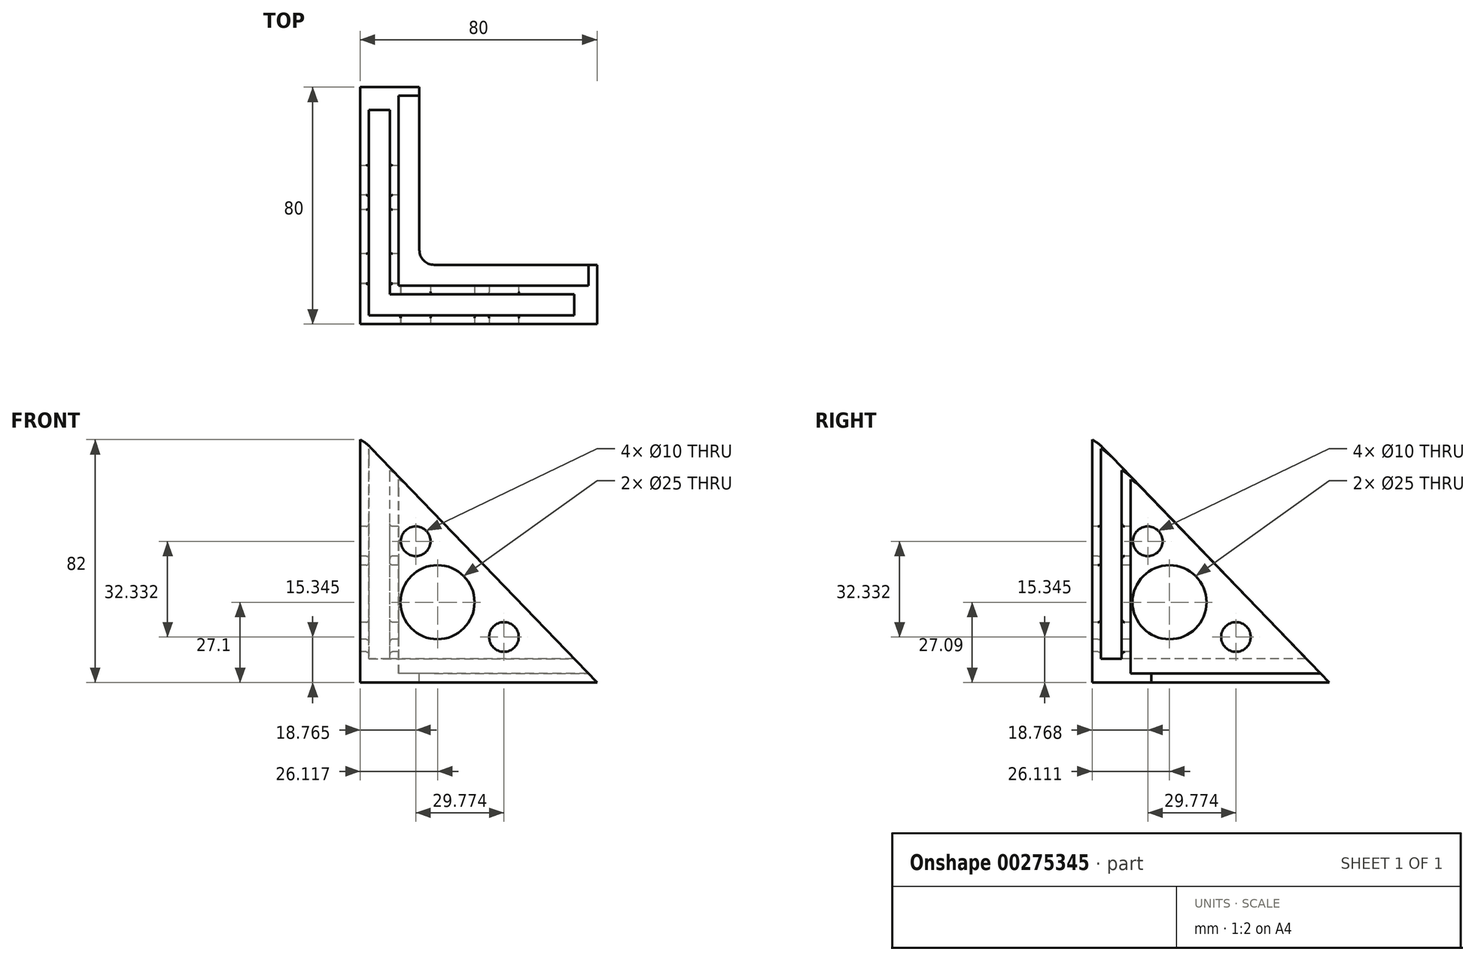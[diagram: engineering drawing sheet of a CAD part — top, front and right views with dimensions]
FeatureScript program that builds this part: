
annotation { "Feature Type Name" : "Feature", "Feature Type Description" : "" }
export const myFeature = defineFeature(function(context is Context, id is Id, definition is map)
    precondition{}
    {
        {
            var Q0;
            Q0=qCreatedBy(makeId("Top.planeOp"),FACE);
            var sketch = newSketch(context, id + "F0", { "sketchPlane" : qUnion([Q0])});
            skLineSegment(sketch, "E0", {"start": v(-54.23, 39.63) * mm, "end": v(-54.23, -40.37) * mm});
            skLineSegment(sketch, "E1", {"start": v(-54.23, -40.37) * mm, "end": v(25.77, -40.37) * mm});
            skLineSegment(sketch, "E2", {"start": v(-54.23, 39.63) * mm, "end": v(-41.23, 39.63) * mm});
            skLineSegment(sketch, "E3", {"start": v(25.77, -40.37) * mm, "end": v(25.77, -27.37) * mm});
            skLineSegment(sketch, "E4", {"start": v(25.77, -27.37) * mm, "end": v(-41.23, -27.37) * mm});
            skLineSegment(sketch, "E5", {"start": v(-41.23, -27.37) * mm, "end": v(-41.23, 39.63) * mm});
            skSolve(sketch);
        }
        {
            var Q0;
            Q0=qSketchRegion(id+"F0",true);
            extrude(context, id + "F1", {"entities" : qUnion([Q0]), "oppositeDirection" : true, "depth" : 80 * mm});
        }
        {
            var Q0;
            Q0=makeQuery(id+"F1.opExtrude","CAP_FACE",FACE,{"disambiguationData":[OSD([sQuery(id+"F0.wireOp",EDGE,"E0"),sQuery(id+"F0.wireOp",EDGE,"E1"),sQuery(id+"F0.wireOp",EDGE,"E2"),sQuery(id+"F0.wireOp",EDGE,"E3"),sQuery(id+"F0.wireOp",EDGE,"E4"),sQuery(id+"F0.wireOp",EDGE,"E5")])],"isStart":true});
            var sketch = newSketch(context, id + "F2", { "sketchPlane" : qUnion([Q0])});
            skLineSegment(sketch, "E6", {"start": v(-51.23, 39.63) * mm, "end": v(-51.23, -37.37) * mm});
            skLineSegment(sketch, "E7", {"start": v(-51.23, -37.37) * mm, "end": v(25.77, -37.37) * mm});
            skLineSegment(sketch, "E8", {"start": v(25.77, -37.37) * mm, "end": v(25.77, -30.37) * mm});
            skLineSegment(sketch, "E9", {"start": v(25.77, -30.37) * mm, "end": v(-44.23, -30.37) * mm});
            skLineSegment(sketch, "E10", {"start": v(-44.23, -30.37) * mm, "end": v(-44.23, 39.63) * mm});
            skLineSegment(sketch, "E11", {"start": v(-44.23, 39.63) * mm, "end": v(-51.23, 39.63) * mm});
            skSolve(sketch);
        }
        {
            var Q0;
            Q0=qSketchRegion(id+"F2",true);
            extrude(context, id + "F3", {"entities" : qUnion([Q0]), "operationType" : NewBodyOperationType.REMOVE, "oppositeDirection" : true, "depth" : 75 * mm});
        }
        {
            var Q0;
            Q0=makeQuery(id+"F1.opExtrude","SWEPT_FACE",FACE,{"disambiguationData":[OSD([sQuery(id+"F0.wireOp",EDGE,"E3")])]});
            var sketch = newSketch(context, id + "F4", { "sketchPlane" : qUnion([Q0])});
            skLineSegment(sketch, "E12.bottom", {"start": v(-40.37, -80) * mm, "end": v(-27.37, -80) * mm});
            skLineSegment(sketch, "E12.top", {"start": v(-40.37, -80) * mm, "end": v(-27.37, -80) * mm});
            skLineSegment(sketch, "E12.left", {"start": v(-40.37, -80) * mm, "end": v(-40.37, -80) * mm});
            skLineSegment(sketch, "E12.right", {"start": v(-27.37, -80) * mm, "end": v(-27.37, -80) * mm});
            skLineSegment(sketch, "E13.bottom", {"start": v(-20.37, -80) * mm, "end": v(-40.37, -80) * mm});
            skLineSegment(sketch, "E13.top", {"start": v(9.63, -93) * mm, "end": v(-40.37, -93) * mm});
            skLineSegment(sketch, "E13.right", {"start": v(-40.37, -80) * mm, "end": v(-40.37, -93) * mm});
            skLineSegment(sketch, "E14", {"start": v(-35.37, -83) * mm, "end": v(-35.37, -90) * mm});
            skLineSegment(sketch, "E15", {"start": v(-35.37, -90) * mm, "end": v(9.63, -90) * mm});
            skLineSegment(sketch, "E16", {"start": v(9.63, -90) * mm, "end": v(9.63, -93) * mm});
            skLineSegment(sketch, "E17", {"start": v(-20.37, -80) * mm, "end": v(-20.37, -83) * mm});
            skLineSegment(sketch, "E18", {"start": v(-20.37, -83) * mm, "end": v(-35.37, -83) * mm});
            skSolve(sketch);
        }
        {
            var Q0;
            Q0=qSketchRegion(id+"F4",true);
            extrude(context, id + "F5", {"entities" : qUnion([Q0]), "operationType" : NewBodyOperationType.ADD, "oppositeDirection" : true, "depth" : 80 * mm});
        }
        {
            var Q0;
            Q0=makeQuery(id+"F1.opExtrude","SWEPT_FACE",FACE,{"disambiguationData":[OSD([sQuery(id+"F0.wireOp",EDGE,"E2")])]});
            var sketch = newSketch(context, id + "F6", { "sketchPlane" : qUnion([Q0])});
            skLineSegment(sketch, "E19.bottom", {"start": v(34.23, -80) * mm, "end": v(54.23, -80) * mm});
            skLineSegment(sketch, "E19.top", {"start": v(41.23, -93) * mm, "end": v(54.23, -93) * mm});
            skLineSegment(sketch, "E19.right", {"start": v(54.23, -80) * mm, "end": v(54.23, -93) * mm});
            skLineSegment(sketch, "E20", {"start": v(34.23, -80) * mm, "end": v(34.23, -83) * mm});
            skLineSegment(sketch, "E21", {"start": v(34.23, -83) * mm, "end": v(49.23, -83) * mm});
            skLineSegment(sketch, "E22", {"start": v(49.23, -83) * mm, "end": v(49.23, -90) * mm});
            skLineSegment(sketch, "E23", {"start": v(49.23, -90) * mm, "end": v(5.33, -90) * mm});
            skLineSegment(sketch, "E24", {"start": v(5.33, -90) * mm, "end": v(5.33, -93) * mm});
            skLineSegment(sketch, "E25", {"start": v(5.33, -93) * mm, "end": v(41.23, -93) * mm});
            skSolve(sketch);
        }
        {
            var Q0;
            Q0=qSketchRegion(id+"F6",true);
            extrude(context, id + "F7", {"entities" : qUnion([Q0]), "operationType" : NewBodyOperationType.ADD, "oppositeDirection" : true, "depth" : 80 * mm});
        }
        {
            var Q0;
            Q0=makeQuery(id+"F7.boolean.opBoolean","MERGE",FACE,{"derivedFrom":[makeQuery(id+"F5.opExtrude","SWEPT_FACE",FACE,{"disambiguationData":[OSD([sQuery(id+"F4.wireOp",EDGE,"E18")])]}),makeQuery(id+"F7.opExtrude","SWEPT_FACE",FACE,{"disambiguationData":[OSD([sQuery(id+"F6.wireOp",EDGE,"E21")])]})]});
            cPlane(context, id + "F8", {"entities" : qUnion([Q0]), "cplaneType" : CPlaneType.OFFSET, "offset" : 0 * mm, "width" : 150 * mm, "height" : 150 * mm});
        }
        {
            var Q0;
            Q0=qCreatedBy(id+"F8.planeOp",FACE);
            var sketch = newSketch(context, id + "F9", { "sketchPlane" : qUnion([Q0])});
            skLineSegment(sketch, "E26.bottom", {"start": v(29.9, 62.36) * mm, "end": v(-66.47, 62.36) * mm});
            skLineSegment(sketch, "E26.top", {"start": v(29.9, -86.56) * mm, "end": v(-66.47, -86.56) * mm});
            skLineSegment(sketch, "E26.left", {"start": v(29.9, 62.36) * mm, "end": v(29.9, -86.56) * mm});
            skLineSegment(sketch, "E26.right", {"start": v(-66.47, 62.36) * mm, "end": v(-66.47, -86.56) * mm});
            skSolve(sketch);
        }
        {
            var Q0;
            Q0=makeQuery(id+"F9.imprint","IMPRINT",FACE,{"disambiguationData":[TD([[makeQuery(id+"F9.imprint","IMPRINT",EDGE,{"derivedFrom":sQuery(id+"F9.wireOp",EDGE,"E26.bottom")}),1.0]])]});
            extrude(context, id + "F10", {"entities" : qUnion([Q0]), "operationType" : NewBodyOperationType.REMOVE, "depth" : 25 * mm});
        }
        {
            var Q0;
            Q0=makeQuery(id+"F5.boolean.opBoolean","MERGE",FACE,{"derivedFrom":[makeQuery(id+"F1.opExtrude","SWEPT_FACE",FACE,{"disambiguationData":[OSD([sQuery(id+"F0.wireOp",EDGE,"E1")])]}),makeQuery(id+"F5.opExtrude","SWEPT_FACE",FACE,{"disambiguationData":[OSD([sQuery(id+"F4.wireOp",EDGE,"E13.right")])]})]});
            var sketch = newSketch(context, id + "F11", { "sketchPlane" : qUnion([Q0])});
            skLineSegment(sketch, "E27", {"start": v(-54.23, 0) * mm, "end": v(25.77, -83) * mm});
            skLineSegment(sketch, "E28", {"start": v(25.77, -83) * mm, "end": v(25.77, 0) * mm});
            skLineSegment(sketch, "E29", {"start": v(25.77, 0) * mm, "end": v(-54.23, 0) * mm});
            skLineSegment(sketch, "E30", {"start": v(-54.23, -83) * mm, "end": v(-14.23, -41.5) * mm});
            skCircle(sketch, "E31", {"center": v(-28.11, -55.9) * mm, "radius": 12.5 * mm});
            skCircle(sketch, "E32", {"center": v(-35.46, -35.32) * mm, "radius": 5 * mm});
            skCircle(sketch, "E33", {"center": v(-5.7, -67.66) * mm, "radius": 5 * mm});
            skSolve(sketch);
        }
        {
            var Q0;
            Q0 = qSketchRegion(id + "F11", true);
            extrude(context, id + "F12", {"entities" : qUnion([Q0]), "operationType" : NewBodyOperationType.REMOVE, "oppositeDirection" : true, "depth" : 13 * mm});
        }
        {
            var Q0;
            {var subQ2=sQuery(id+"F11.wireOp",EDGE,"E27");Q0=makeQuery(id+"F12.boolean.opBoolean","COPY",FACE,{"disambiguationData":[TD([makeQuery(id+"F1.opExtrude","SWEPT_FACE",FACE,{"disambiguationData":[OSD([sQuery(id+"F0.wireOp",EDGE,"E3")])]})])],"derivedFrom":makeQuery(id+"F12.opExtrude","CAP_FACE",FACE,{"disambiguationData":[OSD([subQ2,sQuery(id+"F11.wireOp",EDGE,"E28"),sQuery(id+"F11.wireOp",EDGE,"E29")])],"isStart":false})});}
            var sketch = newSketch(context, id + "F13", { "sketchPlane" : qUnion([Q0])});
            skLineSegment(sketch, "E34", {"start": v(22.88, -80) * mm, "end": v(25.77, -80) * mm});
            skLineSegment(sketch, "E35", {"start": v(25.77, -80) * mm, "end": v(25.77, -83) * mm});
            skLineSegment(sketch, "E36", {"start": v(25.77, -83) * mm, "end": v(22.88, -80) * mm});
            skSolve(sketch);
        }
        {
            var Q0;
            Q0 = qSketchRegion(id + "F13", true);
            extrude(context, id + "F14", {"entities" : qUnion([Q0]), "operationType" : NewBodyOperationType.REMOVE, "oppositeDirection" : true, "depth" : 25 * mm});
        }
        {
            var Q0;
            Q0=makeQuery(id+"F7.boolean.opBoolean","MERGE",FACE,{"derivedFrom":[makeQuery(id+"F5.boolean.opBoolean","MERGE",FACE,{"derivedFrom":[makeQuery(id+"F1.opExtrude","SWEPT_FACE",FACE,{"disambiguationData":[OSD([sQuery(id+"F0.wireOp",EDGE,"E0")])]}),makeQuery(id+"F5.opExtrude","CAP_FACE",FACE,{"disambiguationData":[OSD([sQuery(id+"F4.wireOp",EDGE,"E13.bottom"),sQuery(id+"F4.wireOp",EDGE,"E13.top"),sQuery(id+"F4.wireOp",EDGE,"E13.right"),sQuery(id+"F4.wireOp",EDGE,"E14"),sQuery(id+"F4.wireOp",EDGE,"E15"),sQuery(id+"F4.wireOp",EDGE,"E16"),sQuery(id+"F4.wireOp",EDGE,"E17"),sQuery(id+"F4.wireOp",EDGE,"E18")])],"isStart":false})]}),makeQuery(id+"F7.opExtrude","SWEPT_FACE",FACE,{"disambiguationData":[OSD([sQuery(id+"F6.wireOp",EDGE,"E19.right")])]})]});
            var sketch = newSketch(context, id + "F15", { "sketchPlane" : qUnion([Q0])});
            skLineSegment(sketch, "E37", {"start": v(40.37, 0) * mm, "end": v(-39.63, -83) * mm});
            skLineSegment(sketch, "E38", {"start": v(-39.63, -83) * mm, "end": v(-39.63, 0) * mm});
            skLineSegment(sketch, "E39", {"start": v(-39.63, 0) * mm, "end": v(40.37, 0) * mm});
            skLineSegment(sketch, "E40", {"start": v(40.37, -83) * mm, "end": v(-39.63, 0) * mm});
            skCircle(sketch, "E41", {"center": v(14.26, -55.9) * mm, "radius": 12.5 * mm});
            skCircle(sketch, "E42", {"center": v(-8.17, -67.66) * mm, "radius": 5 * mm});
            skCircle(sketch, "E43", {"center": v(21.6, -35.32) * mm, "radius": 5 * mm});
            skSolve(sketch);
        }
        {
            var Q0;
            Q0 = qSketchRegion(id + "F15", true);
            extrude(context, id + "F16", {"entities" : qUnion([Q0]), "operationType" : NewBodyOperationType.REMOVE, "oppositeDirection" : true, "depth" : 13 * mm});
        }
        {
            var Q0;
            Q0=makeQuery(id+"F16.boolean.opBoolean","COPY",FACE,{"derivedFrom":makeQuery(id+"F16.opExtrude","CAP_FACE",FACE,{"disambiguationData":[OSD([sQuery(id+"F15.wireOp",EDGE,"E37"),sQuery(id+"F15.wireOp",EDGE,"E38"),sQuery(id+"F15.wireOp",EDGE,"E39")])],"isStart":false})});
            var sketch = newSketch(context, id + "F17", { "sketchPlane" : qUnion([Q0])});
            skLineSegment(sketch, "E44", {"start": v(-39.63, -83) * mm, "end": v(-39.63, -80) * mm});
            skLineSegment(sketch, "E45", {"start": v(-39.63, -80) * mm, "end": v(-36.74, -80) * mm});
            skLineSegment(sketch, "E46", {"start": v(-36.74, -80) * mm, "end": v(-39.63, -83) * mm});
            skSolve(sketch);
        }
        {
            var Q0;
            Q0 = qSketchRegion(id + "F17", true);
            extrude(context, id + "F18", {"entities" : qUnion([Q0]), "operationType" : NewBodyOperationType.REMOVE, "oppositeDirection" : true, "depth" : 25 * mm});
        }
        {
            var Q0;
            Q0=makeQuery(id+"F16.boolean.opBoolean","INTERSECT",EDGE,{"disambiguationData":[OD(1.0)],"derivedFrom":[makeQuery(id+"F14.boolean.opBoolean","MERGE",FACE,{"derivedFrom":[makeQuery(id+"F12.boolean.opBoolean","COPY",FACE,{"derivedFrom":makeQuery(id+"F12.opExtrude","SWEPT_FACE",FACE,{"disambiguationData":[OSD([sQuery(id+"F11.wireOp",EDGE,"E27")])]})}),makeQuery(id+"F14.opExtrude","SWEPT_FACE",FACE,{"disambiguationData":[OSD([sQuery(id+"F13.wireOp",EDGE,"E36")])]})]}),makeQuery(id+"F16.opExtrude","SWEPT_FACE",FACE,{"disambiguationData":[OSD([sQuery(id+"F15.wireOp",EDGE,"E37")])]})]});
            var Q1;
            Q1=makeQuery(id+"F16.boolean.opBoolean","INTERSECT",EDGE,{"disambiguationData":[OD(0.0)],"derivedFrom":[makeQuery(id+"F14.boolean.opBoolean","MERGE",FACE,{"derivedFrom":[makeQuery(id+"F12.boolean.opBoolean","COPY",FACE,{"derivedFrom":makeQuery(id+"F12.opExtrude","SWEPT_FACE",FACE,{"disambiguationData":[OSD([sQuery(id+"F11.wireOp",EDGE,"E27")])]})}),makeQuery(id+"F14.opExtrude","SWEPT_FACE",FACE,{"disambiguationData":[OSD([sQuery(id+"F13.wireOp",EDGE,"E36")])]})]}),makeQuery(id+"F16.opExtrude","SWEPT_FACE",FACE,{"disambiguationData":[OSD([sQuery(id+"F15.wireOp",EDGE,"E37")])]})]});
            var Q2;
            Q2=makeQuery(id+"F7.boolean.opBoolean","INTERSECT",EDGE,{"derivedFrom":[makeQuery(id+"F5.opExtrude","SWEPT_FACE",FACE,{"disambiguationData":[OSD([sQuery(id+"F4.wireOp",EDGE,"E17")])]}),makeQuery(id+"F7.opExtrude","SWEPT_FACE",FACE,{"disambiguationData":[OSD([sQuery(id+"F6.wireOp",EDGE,"E20")])]})]});
            fillet(context, id + "F19", {"entities" : qUnion([Q0, Q1, Q2]), "radius" : 5 * mm, "tangentPropagation" : true, "allowEdgeOverflow" : false});
        }
        {
            var Q0;
            Q0=makeQuery(id+"F12.boolean.opBoolean","COPY",EDGE,{"derivedFrom":makeQuery(id+"F12.opExtrude","CAP_EDGE",EDGE,{"disambiguationData":[OSD([sQuery(id+"F11.wireOp",EDGE,"E32")])],"isStart":false})});
            var Q1;
            Q1=makeQuery(id+"F16.boolean.opBoolean","COPY",EDGE,{"derivedFrom":makeQuery(id+"F16.opExtrude","CAP_EDGE",EDGE,{"disambiguationData":[OSD([sQuery(id+"F15.wireOp",EDGE,"E43")])],"isStart":false})});
            var Q2;
            Q2=makeQuery(id+"F12.boolean.opBoolean","INTERSECT",EDGE,{"derivedFrom":[makeQuery(id+"F3.boolean.opBoolean","COPY",FACE,{"derivedFrom":makeQuery(id+"F3.opExtrude","SWEPT_FACE",FACE,{"disambiguationData":[OSD([sQuery(id+"F2.wireOp",EDGE,"E9")])]})}),makeQuery(id+"F12.opExtrude","SWEPT_FACE",FACE,{"disambiguationData":[OSD([sQuery(id+"F11.wireOp",EDGE,"E32")])]})]});
            var Q3;
            Q3=makeQuery(id+"F16.boolean.opBoolean","INTERSECT",EDGE,{"derivedFrom":[makeQuery(id+"F3.boolean.opBoolean","COPY",FACE,{"derivedFrom":makeQuery(id+"F3.opExtrude","SWEPT_FACE",FACE,{"disambiguationData":[OSD([sQuery(id+"F2.wireOp",EDGE,"E10")])]})}),makeQuery(id+"F16.opExtrude","SWEPT_FACE",FACE,{"disambiguationData":[OSD([sQuery(id+"F15.wireOp",EDGE,"E43")])]})]});
            var Q4;
            Q4=makeQuery(id+"F12.boolean.opBoolean","INTERSECT",EDGE,{"derivedFrom":[makeQuery(id+"F3.boolean.opBoolean","COPY",FACE,{"derivedFrom":makeQuery(id+"F3.opExtrude","SWEPT_FACE",FACE,{"disambiguationData":[OSD([sQuery(id+"F2.wireOp",EDGE,"E7")])]})}),makeQuery(id+"F12.opExtrude","SWEPT_FACE",FACE,{"disambiguationData":[OSD([sQuery(id+"F11.wireOp",EDGE,"E31")])]})]});
            var Q5;
            Q5=makeQuery(id+"F12.boolean.opBoolean","COPY",EDGE,{"derivedFrom":makeQuery(id+"F12.opExtrude","CAP_EDGE",EDGE,{"disambiguationData":[OSD([sQuery(id+"F11.wireOp",EDGE,"E31")])],"isStart":false})});
            var Q6;
            Q6=makeQuery(id+"F16.boolean.opBoolean","COPY",EDGE,{"derivedFrom":makeQuery(id+"F16.opExtrude","CAP_EDGE",EDGE,{"disambiguationData":[OSD([sQuery(id+"F15.wireOp",EDGE,"E41")])],"isStart":false})});
            var Q7;
            Q7=makeQuery(id+"F16.boolean.opBoolean","INTERSECT",EDGE,{"derivedFrom":[makeQuery(id+"F3.boolean.opBoolean","COPY",FACE,{"derivedFrom":makeQuery(id+"F3.opExtrude","SWEPT_FACE",FACE,{"disambiguationData":[OSD([sQuery(id+"F2.wireOp",EDGE,"E10")])]})}),makeQuery(id+"F16.opExtrude","SWEPT_FACE",FACE,{"disambiguationData":[OSD([sQuery(id+"F15.wireOp",EDGE,"E41")])]})]});
            var Q8;
            Q8=makeQuery(id+"F16.boolean.opBoolean","INTERSECT",EDGE,{"derivedFrom":[makeQuery(id+"F3.boolean.opBoolean","COPY",FACE,{"derivedFrom":makeQuery(id+"F3.opExtrude","SWEPT_FACE",FACE,{"disambiguationData":[OSD([sQuery(id+"F2.wireOp",EDGE,"E6")])]})}),makeQuery(id+"F16.opExtrude","SWEPT_FACE",FACE,{"disambiguationData":[OSD([sQuery(id+"F15.wireOp",EDGE,"E41")])]})]});
            var Q9;
            Q9=makeQuery(id+"F16.boolean.opBoolean","COPY",EDGE,{"derivedFrom":makeQuery(id+"F16.opExtrude","CAP_EDGE",EDGE,{"disambiguationData":[OSD([sQuery(id+"F15.wireOp",EDGE,"E41")])],"isStart":true})});
            var Q10;
            Q10=makeQuery(id+"F12.boolean.opBoolean","COPY",EDGE,{"derivedFrom":makeQuery(id+"F12.opExtrude","CAP_EDGE",EDGE,{"disambiguationData":[OSD([sQuery(id+"F11.wireOp",EDGE,"E31")])],"isStart":true})});
            var Q11;
            Q11=makeQuery(id+"F16.boolean.opBoolean","COPY",EDGE,{"derivedFrom":makeQuery(id+"F16.opExtrude","CAP_EDGE",EDGE,{"disambiguationData":[OSD([sQuery(id+"F15.wireOp",EDGE,"E42")])],"isStart":true})});
            var Q12;
            Q12=makeQuery(id+"F16.boolean.opBoolean","INTERSECT",EDGE,{"derivedFrom":[makeQuery(id+"F3.boolean.opBoolean","COPY",FACE,{"derivedFrom":makeQuery(id+"F3.opExtrude","SWEPT_FACE",FACE,{"disambiguationData":[OSD([sQuery(id+"F2.wireOp",EDGE,"E6")])]})}),makeQuery(id+"F16.opExtrude","SWEPT_FACE",FACE,{"disambiguationData":[OSD([sQuery(id+"F15.wireOp",EDGE,"E42")])]})]});
            var Q13;
            Q13=makeQuery(id+"F16.boolean.opBoolean","INTERSECT",EDGE,{"derivedFrom":[makeQuery(id+"F3.boolean.opBoolean","COPY",FACE,{"derivedFrom":makeQuery(id+"F3.opExtrude","SWEPT_FACE",FACE,{"disambiguationData":[OSD([sQuery(id+"F2.wireOp",EDGE,"E10")])]})}),makeQuery(id+"F16.opExtrude","SWEPT_FACE",FACE,{"disambiguationData":[OSD([sQuery(id+"F15.wireOp",EDGE,"E42")])]})]});
            var Q14;
            Q14=makeQuery(id+"F16.boolean.opBoolean","COPY",EDGE,{"derivedFrom":makeQuery(id+"F16.opExtrude","CAP_EDGE",EDGE,{"disambiguationData":[OSD([sQuery(id+"F15.wireOp",EDGE,"E42")])],"isStart":false})});
            var Q15;
            Q15=makeQuery(id+"F12.boolean.opBoolean","INTERSECT",EDGE,{"derivedFrom":[makeQuery(id+"F3.boolean.opBoolean","COPY",FACE,{"derivedFrom":makeQuery(id+"F3.opExtrude","SWEPT_FACE",FACE,{"disambiguationData":[OSD([sQuery(id+"F2.wireOp",EDGE,"E7")])]})}),makeQuery(id+"F12.opExtrude","SWEPT_FACE",FACE,{"disambiguationData":[OSD([sQuery(id+"F11.wireOp",EDGE,"E33")])]})]});
            var Q16;
            Q16=makeQuery(id+"F12.boolean.opBoolean","COPY",EDGE,{"derivedFrom":makeQuery(id+"F12.opExtrude","CAP_EDGE",EDGE,{"disambiguationData":[OSD([sQuery(id+"F11.wireOp",EDGE,"E33")])],"isStart":true})});
            var Q17;
            Q17=makeQuery(id+"F12.boolean.opBoolean","INTERSECT",EDGE,{"derivedFrom":[makeQuery(id+"F3.boolean.opBoolean","COPY",FACE,{"derivedFrom":makeQuery(id+"F3.opExtrude","SWEPT_FACE",FACE,{"disambiguationData":[OSD([sQuery(id+"F2.wireOp",EDGE,"E9")])]})}),makeQuery(id+"F12.opExtrude","SWEPT_FACE",FACE,{"disambiguationData":[OSD([sQuery(id+"F11.wireOp",EDGE,"E33")])]})]});
            var Q18;
            Q18=makeQuery(id+"F12.boolean.opBoolean","COPY",EDGE,{"derivedFrom":makeQuery(id+"F12.opExtrude","CAP_EDGE",EDGE,{"disambiguationData":[OSD([sQuery(id+"F11.wireOp",EDGE,"E33")])],"isStart":false})});
            var Q19;
            {var subQ0=sQuery(id+"F11.wireOp",EDGE,"E27");Q19=makeQuery(id+"F12.boolean.opBoolean","COPY",EDGE,{"disambiguationData":[topologyDisambiguationEdgeConnected([makeQuery(id+"F1.opExtrude","SWEPT_FACE",FACE,{"disambiguationData":[OSD([sQuery(id+"F0.wireOp",EDGE,"E4")])]}),makeQuery(id+"F12.opExtrude","SWEPT_FACE",FACE,{"disambiguationData":[OSD([subQ0])]})])],"derivedFrom":makeQuery(id+"F12.opExtrude","CAP_EDGE",EDGE,{"disambiguationData":[OSD([subQ0])],"isStart":false})});}
            var Q20;
            {var subQ0=sQuery(id+"F15.wireOp",EDGE,"E37");Q20=makeQuery(id+"F16.boolean.opBoolean","COPY",EDGE,{"disambiguationData":[topologyDisambiguationEdgeConnected([makeQuery(id+"F1.opExtrude","SWEPT_FACE",FACE,{"disambiguationData":[OSD([sQuery(id+"F0.wireOp",EDGE,"E5")])]})])],"derivedFrom":makeQuery(id+"F16.opExtrude","CAP_EDGE",EDGE,{"disambiguationData":[OSD([subQ0])],"isStart":false})});}
            var Q21;
            Q21=makeQuery(id+"F16.boolean.opBoolean","INTERSECT",EDGE,{"derivedFrom":[makeQuery(id+"F3.boolean.opBoolean","COPY",FACE,{"derivedFrom":makeQuery(id+"F3.opExtrude","SWEPT_FACE",FACE,{"disambiguationData":[OSD([sQuery(id+"F2.wireOp",EDGE,"E6")])]})}),makeQuery(id+"F16.opExtrude","SWEPT_FACE",FACE,{"disambiguationData":[OSD([sQuery(id+"F15.wireOp",EDGE,"E43")])]})]});
            var Q22;
            Q22=makeQuery(id+"F16.boolean.opBoolean","COPY",EDGE,{"derivedFrom":makeQuery(id+"F16.opExtrude","CAP_EDGE",EDGE,{"disambiguationData":[OSD([sQuery(id+"F15.wireOp",EDGE,"E43")])],"isStart":true})});
            var Q23;
            Q23=makeQuery(id+"F12.boolean.opBoolean","INTERSECT",EDGE,{"derivedFrom":[makeQuery(id+"F3.boolean.opBoolean","COPY",FACE,{"derivedFrom":makeQuery(id+"F3.opExtrude","SWEPT_FACE",FACE,{"disambiguationData":[OSD([sQuery(id+"F2.wireOp",EDGE,"E7")])]})}),makeQuery(id+"F12.opExtrude","SWEPT_FACE",FACE,{"disambiguationData":[OSD([sQuery(id+"F11.wireOp",EDGE,"E32")])]})]});
            var Q24;
            Q24=makeQuery(id+"F12.boolean.opBoolean","COPY",EDGE,{"derivedFrom":makeQuery(id+"F12.opExtrude","CAP_EDGE",EDGE,{"disambiguationData":[OSD([sQuery(id+"F11.wireOp",EDGE,"E32")])],"isStart":true})});
            var Q25;
            Q25=makeQuery(id+"F16.boolean.opBoolean","COPY",EDGE,{"derivedFrom":makeQuery(id+"F16.opExtrude","CAP_EDGE",EDGE,{"disambiguationData":[OSD([sQuery(id+"F15.wireOp",EDGE,"E37")])],"isStart":true})});
            var Q26;
            Q26=makeQuery(id+"F12.boolean.opBoolean","COPY",EDGE,{"derivedFrom":makeQuery(id+"F12.opExtrude","CAP_EDGE",EDGE,{"disambiguationData":[OSD([sQuery(id+"F11.wireOp",EDGE,"E27")])],"isStart":true})});
            fillet(context, id + "F20", {"entities" : qUnion([Q0, Q1, Q2, Q3, Q4, Q5, Q6, Q7, Q8, Q9, Q10, Q11, Q12, Q13, Q14, Q15, Q16, Q17, Q18, Q19, Q20, Q21, Q22, Q23, Q24, Q25, Q26]), "radius" : 1 * mm, "tangentPropagation" : true, "allowEdgeOverflow" : false});
        }
    });
